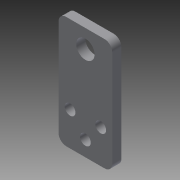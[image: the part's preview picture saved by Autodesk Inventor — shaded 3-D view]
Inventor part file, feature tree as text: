
AUTODESK INVENTOR PART (.ipt)
format: ipt  version: 2015 SP1 (Build 190203100, 203)  size: 105,472 bytes
history: native  units: in
note: dims shown in document units (in); Inventor stores cm internally (conversion verified against a paired STEP export)
features: extrude x1, fillet x1, sketch x1
ambient origin geometry x8: Origin, YZ Plane, XZ Plane, XY Plane, X Axis, Y Axis, Z Axis, Center Point
bodies: Body1 (feature_tree)
feature tree (3):
  extrude  "Extrusion3"  Depth=0.1969in
  fillet  "Fillet2"  Radius=0.2756in
  sketch  "Sketch1"  dims[d3=1.378in d4=0.2756in d5=0.2756in d6=0.2756in d9=0.3937in d12=0.4724in d13=0.4724in d22=0.2362in d23=0.0in d24=0.1969in d32=0.7874in d33=0.4724in d34=1.5354in]
